# Revit family: Gira_207000
name_source: partatom
category: Elektroinstallationen
revit_build: Autodesk Revit 2017 (Build: 20160225_1515(x64)
units: mm (PartAtom-declared; Revit-internal decimal feet)

## family parameters
Basisbauteil = Fläche
Beim Laden mit Abzugskörper schneiden = Nein
Bemaßung runder Anschluss = Durchmesser verwenden
Beschriftungsausrichtung beibehalten = Nein
Gemeinsam genutzt = Nein
Raumberechnungspunkt = Nein
Teiletyp = Normal

## types (1)
- Gira_207000
    Andere Bussysteme = ohne
    BIM = https://media.stage.bim.site X1 REG KNX.rfa
    Beschreibung = Gira L1  REG Merkmale: - Logikfunktionen:   Funktionsvielfalt durch Bausteinbibliothek mit 36 Logikbausteinen (z. B. Mathematische Grundfunktionen, sonnenstandsgeführte Rollladen- und Jalousie-Steuerung, Temperatur-Regelung, Trennwandsteuerung, Treppenhauslicht, Zufallsgenerator). - Konfigurierbare Logikbausteine (z. B. frei wählbare Anzahl der Eingänge). - Einfache Parametrierung von Zeitschaltuhren und Szenen:   bis zu 20 Zeitschaltuhren mit jeweils 10 Schaltzeiten.   bis zu 20 Szenen-Sets mit jeweils 64 Szenen. - Bis zu 480 Datenpunkte in einem Projekt verwendbar   (300 KNX Gruppenadressdatenpunkte, 180 frei verfügbare Gerätedatenpunkte). - Interkomfunktion um Werte z. B. zwischen einem weiteren L1 oder einem X1 über Ethernet auszutauschen. - Optimierte Inbetriebnahme:   schnelle Projektänderung oder -aktualisierung im laufenden Betrieb ohne Geräteneustart möglich. - Zwei Buchsen RJ45 mit Switch-Funktionalität unterstützen das einfache Durchschleifen des Patchkabels. - Hohe Sicherheit:   Die verschlüsselte TLS-Datenübertragung zwischen GPA und Gira L1 verhindert das Mitlesen durch Dritte.   Das Geräte-Passwort schützt den Gira L1 vor Fremdzugriff. - Projektsicherung: Speichern einer Projektkopie auf dem Gira L1. - Inbetriebnahme:   Physikalische Adresse und Applikation werden mit der KNX Inbetriebnahme-Software ETS ab der Version 4.1.8 parametriert.   Die weitere Projektierung erfolgt über den Gira Projekt Assistenten (GPA). Der Gira Projekt Assistent ist kostenlos im Gira Downloadbereich verfügbar. - Funktionale Erweiterungen bzw. Aktualisierungen über Firmware- und Software-Updates. - Hardware für KNX Secure vorbereitet. Zukünftiges Firmware-Update erforderlich.  Hinweise : - Versorgung über externe DC 24 V.
    Bussystem Funkbus = Nein
    Bussystem KNX = Ja
    Bussystem KNX-Funk = Nein
    Bussystem LON = Nein
    Bussystem Powernet = Nein
    Datenblatt = https://katalog.gira.de
    GTIN = 4010337016717
    HAN = 207000
    Hersteller = Gira
    Logischer Baustein = Ja
    Mit Busankopplung = Nein
    Montageart = REG
    Produktseite = http://katalog.gira.de
    Typname = Gira L1 KNX REG
    URL = https://www.gira.de
    Vorgabe-Ansicht = 1219 mm

## geometry (parser evidence)
native form markers: Sweep x2
no freeform markers — native parametric forms only
